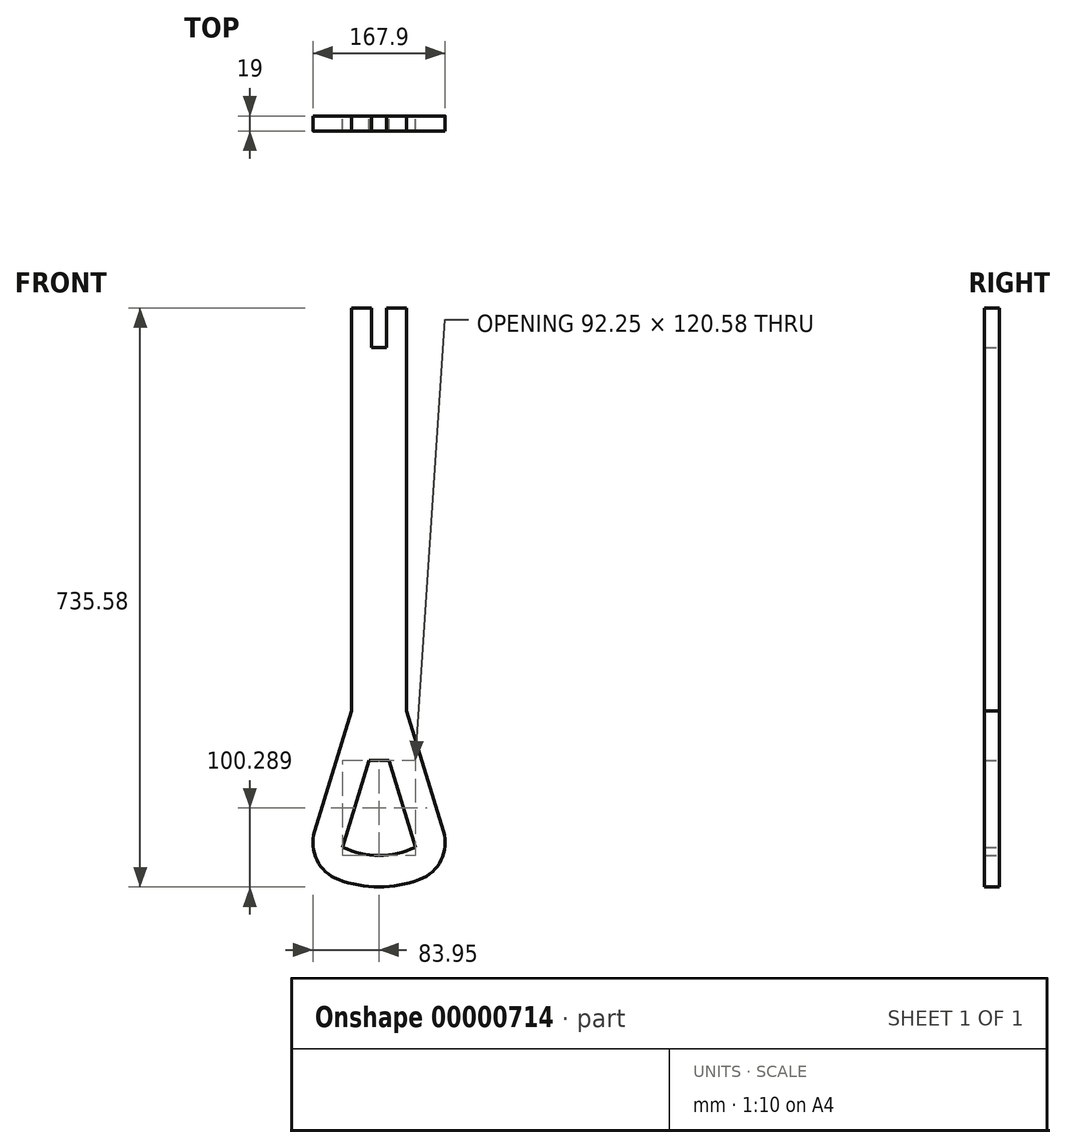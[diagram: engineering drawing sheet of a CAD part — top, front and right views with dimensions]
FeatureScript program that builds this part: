
annotation { "Feature Type Name" : "Feature", "Feature Type Description" : "" }
export const myFeature = defineFeature(function(context is Context, id is Id, definition is map)
    precondition{}
    {
        {
            var Q0;
            Q0=qCreatedBy(makeId("Front.planeOp"),FACE);
            var sketch = newSketch(context, id + "F0", { "sketchPlane" : qUnion([Q0])});
            skLineSegment(sketch, "E0", {"start": v(-12.5, 50) * mm, "end": v(12.5, 50) * mm});
            skLineSegment(sketch, "E1", {"start": v(0, 50) * mm, "end": v(0, 0) * mm, "construction": true});
            skLineSegment(sketch, "E2", {"start": v(-12.5, 50) * mm, "end": v(-46.12, -59.98) * mm});
            skLineSegment(sketch, "E3", {"start": v(12.5, 50) * mm, "end": v(46.12, -59.98) * mm});
            skArc(sketch, "E4", {"start": v(-46.12, -59.98) * mm, "mid": v(0, -70.58) * mm, "end": v(46.12, -59.98) * mm});
            skArc(sketch, "E5", {"start": v(-51.7, -101.1) * mm, "mid": v(0, -110.58) * mm, "end": v(51.7, -101.1) * mm});
            skLineSegment(sketch, "E6", {"start": v(-81.76, -39.73) * mm, "end": v(-35, 113.22) * mm});
            skLineSegment(sketch, "E7", {"start": v(-35, 113.22) * mm, "end": v(-35, 625) * mm});
            skLineSegment(sketch, "E8", {"start": v(-35, 625) * mm, "end": v(-9.5, 625) * mm});
            skLineSegment(sketch, "E9", {"start": v(35, 625) * mm, "end": v(35, 113.22) * mm});
            skLineSegment(sketch, "E10", {"start": v(35, 113.22) * mm, "end": v(81.76, -39.73) * mm});
            skPoint(sketch, "E11.visualSharp", {"position": v(-93.13, -76.9) * mm});
            skArc(sketch, "E11.filletArc", {"start": v(-81.76, -39.73) * mm, "mid": v(-78.85, -76.35) * mm, "end": v(-51.7, -101.1) * mm});
            skPoint(sketch, "E12.visualSharp", {"position": v(93.13, -76.9) * mm});
            skArc(sketch, "E12.filletArc", {"start": v(51.7, -101.1) * mm, "mid": v(78.85, -76.35) * mm, "end": v(81.76, -39.73) * mm});
            skLineSegment(sketch, "E13.top", {"start": v(-9.5, 575) * mm, "end": v(9.5, 575) * mm});
            skLineSegment(sketch, "E13.left", {"start": v(-9.5, 625) * mm, "end": v(-9.5, 575) * mm});
            skLineSegment(sketch, "E13.right", {"start": v(9.5, 625) * mm, "end": v(9.5, 575) * mm});
            skLineSegment(sketch, "E14", {"start": v(0, 575) * mm, "end": v(0, 50) * mm, "construction": true});
            skLineSegment(sketch, "E15.trimOffspring", {"start": v(9.5, 625) * mm, "end": v(35, 625) * mm});
            skSolve(sketch);
        }
        {
            var Q0;
            Q0=makeQuery(id+"F0.imprint","IMPRINT",FACE,{"disambiguationData":[TD([[makeQuery(id+"F0.imprint","IMPRINT",EDGE,{"derivedFrom":sQuery(id+"F0.wireOp",EDGE,"E0")}),1.0]])]});
            extrude(context, id + "F1", {"entities" : qUnion([Q0]), "depth" : 19 * mm});
        }
    });
